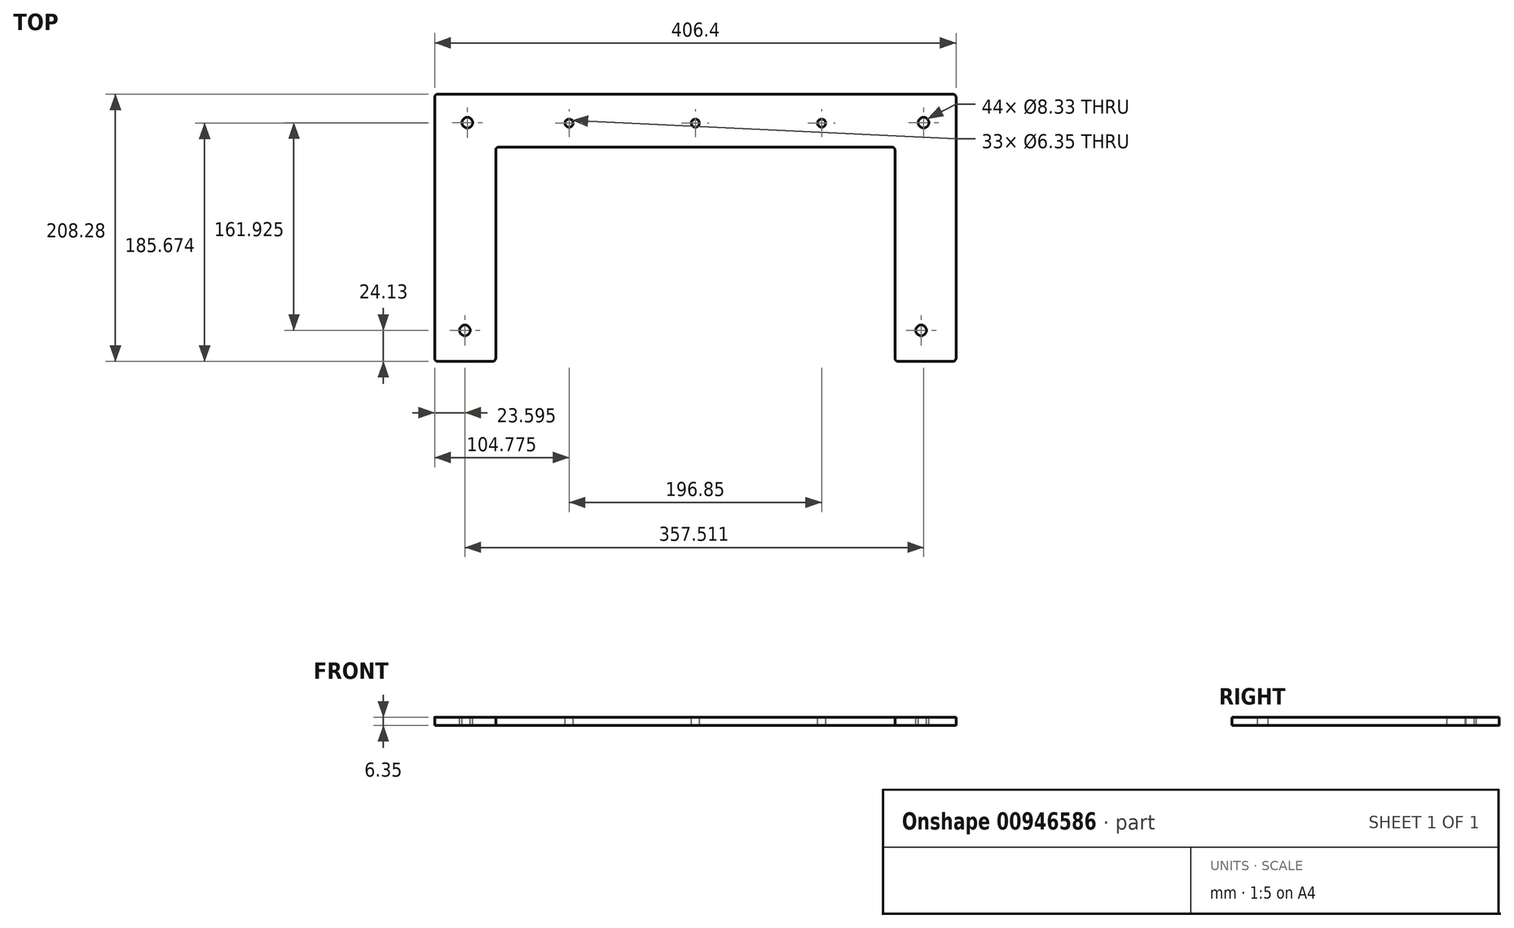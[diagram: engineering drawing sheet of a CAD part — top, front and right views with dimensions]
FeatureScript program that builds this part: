
annotation { "Feature Type Name" : "Feature", "Feature Type Description" : "" }
export const myFeature = defineFeature(function(context is Context, id is Id, definition is map)
    precondition{}
    {
        {
            var Q0;
            Q0=qCreatedBy(makeId("Top.planeOp"),FACE);
            var sketch = newSketch(context, id + "F0", { "sketchPlane" : qUnion([Q0])});
            skLineSegment(sketch, "E0", {"start": v(-203.2, 0) * mm, "end": v(203.2, 0) * mm});
            skLineSegment(sketch, "E1", {"start": v(0, 45.8) * mm, "end": v(0, -43.22) * mm, "construction": true});
            skLineSegment(sketch, "E2", {"start": v(-203.2, 0) * mm, "end": v(-203.2, -208.28) * mm});
            skLineSegment(sketch, "E3", {"start": v(-203.2, -208.28) * mm, "end": v(-155.58, -208.28) * mm});
            skLineSegment(sketch, "E4", {"start": v(-155.58, -208.28) * mm, "end": v(-155.58, -41.15) * mm});
            skLineSegment(sketch, "E5", {"start": v(-155.58, -41.15) * mm, "end": v(155.58, -41.15) * mm});
            skLineSegment(sketch, "E6", {"start": v(155.58, -41.15) * mm, "end": v(155.58, -208.28) * mm});
            skLineSegment(sketch, "E7", {"start": v(155.58, -208.28) * mm, "end": v(203.2, -208.28) * mm});
            skLineSegment(sketch, "E8", {"start": v(203.2, -208.28) * mm, "end": v(203.2, 0) * mm});
            skSolve(sketch);
        }
        {
            var Q0;
            Q0 = qSketchRegion(id + "F0", true);
            extrude(context, id + "F1", {"entities" : qUnion([Q0]), "depth" : 6.35 * mm, "offsetDistance" : 25.4 * mm});
        }
        {
            var Q0;
            Q0=makeQuery(id+"F1.opExtrude","SWEPT_EDGE",EDGE,{"disambiguationData":[OSD([sQuery(id+"F0.wireOp",EDGE,"E4"),sQuery(id+"F0.wireOp",EDGE,"E5")])]});
            var Q1;
            Q1=makeQuery(id+"F1.opExtrude","SWEPT_EDGE",EDGE,{"disambiguationData":[OSD([sQuery(id+"F0.wireOp",EDGE,"E5"),sQuery(id+"F0.wireOp",EDGE,"E6")])]});
            var Q2;
            Q2=makeQuery(id+"F1.opExtrude","SWEPT_EDGE",EDGE,{"disambiguationData":[OSD([sQuery(id+"F0.wireOp",EDGE,"E6"),sQuery(id+"F0.wireOp",EDGE,"E7")])]});
            var Q3;
            Q3=makeQuery(id+"F1.opExtrude","SWEPT_EDGE",EDGE,{"disambiguationData":[OSD([sQuery(id+"F0.wireOp",EDGE,"E3"),sQuery(id+"F0.wireOp",EDGE,"E4")])]});
            var Q4;
            Q4=makeQuery(id+"F1.opExtrude","SWEPT_EDGE",EDGE,{"disambiguationData":[OSD([sQuery(id+"F0.wireOp",EDGE,"E2"),sQuery(id+"F0.wireOp",EDGE,"E3")])]});
            var Q5;
            Q5=makeQuery(id+"F1.opExtrude","SWEPT_EDGE",EDGE,{"disambiguationData":[OSD([sQuery(id+"F0.wireOp",EDGE,"E7"),sQuery(id+"F0.wireOp",EDGE,"E8")])]});
            var Q6;
            Q6=makeQuery(id+"F1.opExtrude","SWEPT_EDGE",EDGE,{"disambiguationData":[OSD([sQuery(id+"F0.wireOp",EDGE,"E0"),sQuery(id+"F0.wireOp",EDGE,"E8")])]});
            var Q7;
            Q7=makeQuery(id+"F1.opExtrude","SWEPT_EDGE",EDGE,{"disambiguationData":[OSD([sQuery(id+"F0.wireOp",EDGE,"E0"),sQuery(id+"F0.wireOp",EDGE,"E2")])]});
            fillet(context, id + "F2", {"entities" : qUnion([Q0, Q1, Q2, Q3, Q4, Q5, Q6, Q7]), "radius" : 2.54 * mm, "tangentPropagation" : true, "allowEdgeOverflow" : false});
        }
        {
            var Q0;
            Q0=makeQuery(id+"F1.opExtrude","CAP_FACE",FACE,{"disambiguationData":[OSD([sQuery(id+"F0.wireOp",EDGE,"E0"),sQuery(id+"F0.wireOp",EDGE,"E2"),sQuery(id+"F0.wireOp",EDGE,"E3"),sQuery(id+"F0.wireOp",EDGE,"E4"),sQuery(id+"F0.wireOp",EDGE,"E5"),sQuery(id+"F0.wireOp",EDGE,"E6"),sQuery(id+"F0.wireOp",EDGE,"E7"),sQuery(id+"F0.wireOp",EDGE,"E8")])],"isStart":false});
            var sketch = newSketch(context, id + "F3", { "sketchPlane" : qUnion([Q0])});
            skCircle(sketch, "E9", {"center": v(-177.7, -22.22) * mm, "radius": 4.17 * mm});
            skCircle(sketch, "E10", {"center": v(-179.6, -184.15) * mm, "radius": 4.17 * mm});
            skCircle(sketch, "E11", {"center": v(177.9, -22.22) * mm, "radius": 4.17 * mm});
            skCircle(sketch, "E12", {"center": v(176, -184.15) * mm, "radius": 4.17 * mm});
            skSolve(sketch);
        }
        {
            var Q0;
            Q0 = qSketchRegion(id + "F3", true);
            extrude(context, id + "F4", {"entities" : qUnion([Q0]), "operationType" : NewBodyOperationType.REMOVE, "oppositeDirection" : true, "depth" : 25.4 * mm, "offsetDistance" : 25.4 * mm});
        }
        {
            var Q0;
            Q0=makeQuery(id+"F1.opExtrude","CAP_FACE",FACE,{"disambiguationData":[OSD([sQuery(id+"F0.wireOp",EDGE,"E0"),sQuery(id+"F0.wireOp",EDGE,"E2"),sQuery(id+"F0.wireOp",EDGE,"E3"),sQuery(id+"F0.wireOp",EDGE,"E4"),sQuery(id+"F0.wireOp",EDGE,"E5"),sQuery(id+"F0.wireOp",EDGE,"E6"),sQuery(id+"F0.wireOp",EDGE,"E7"),sQuery(id+"F0.wireOp",EDGE,"E8")])],"isStart":false});
            var sketch = newSketch(context, id + "F5", { "sketchPlane" : qUnion([Q0])});
            skCircle(sketch, "E13", {"center": v(0, -22.6) * mm, "radius": 3.18 * mm});
            skCircle(sketch, "E14", {"center": v(-98.43, -22.6) * mm, "radius": 3.18 * mm});
            skCircle(sketch, "E15", {"center": v(98.43, -22.6) * mm, "radius": 3.18 * mm});
            skLineSegment(sketch, "E16", {"start": v(-98.43, -22.6) * mm, "end": v(133.43, -22.6) * mm, "construction": true});
            skSolve(sketch);
        }
        {
            var Q0;
            Q0 = qSketchRegion(id + "F5", true);
            extrude(context, id + "F6", {"entities" : qUnion([Q0]), "operationType" : NewBodyOperationType.REMOVE, "oppositeDirection" : true, "depth" : 25.4 * mm, "offsetDistance" : 25.4 * mm});
        }
    });
